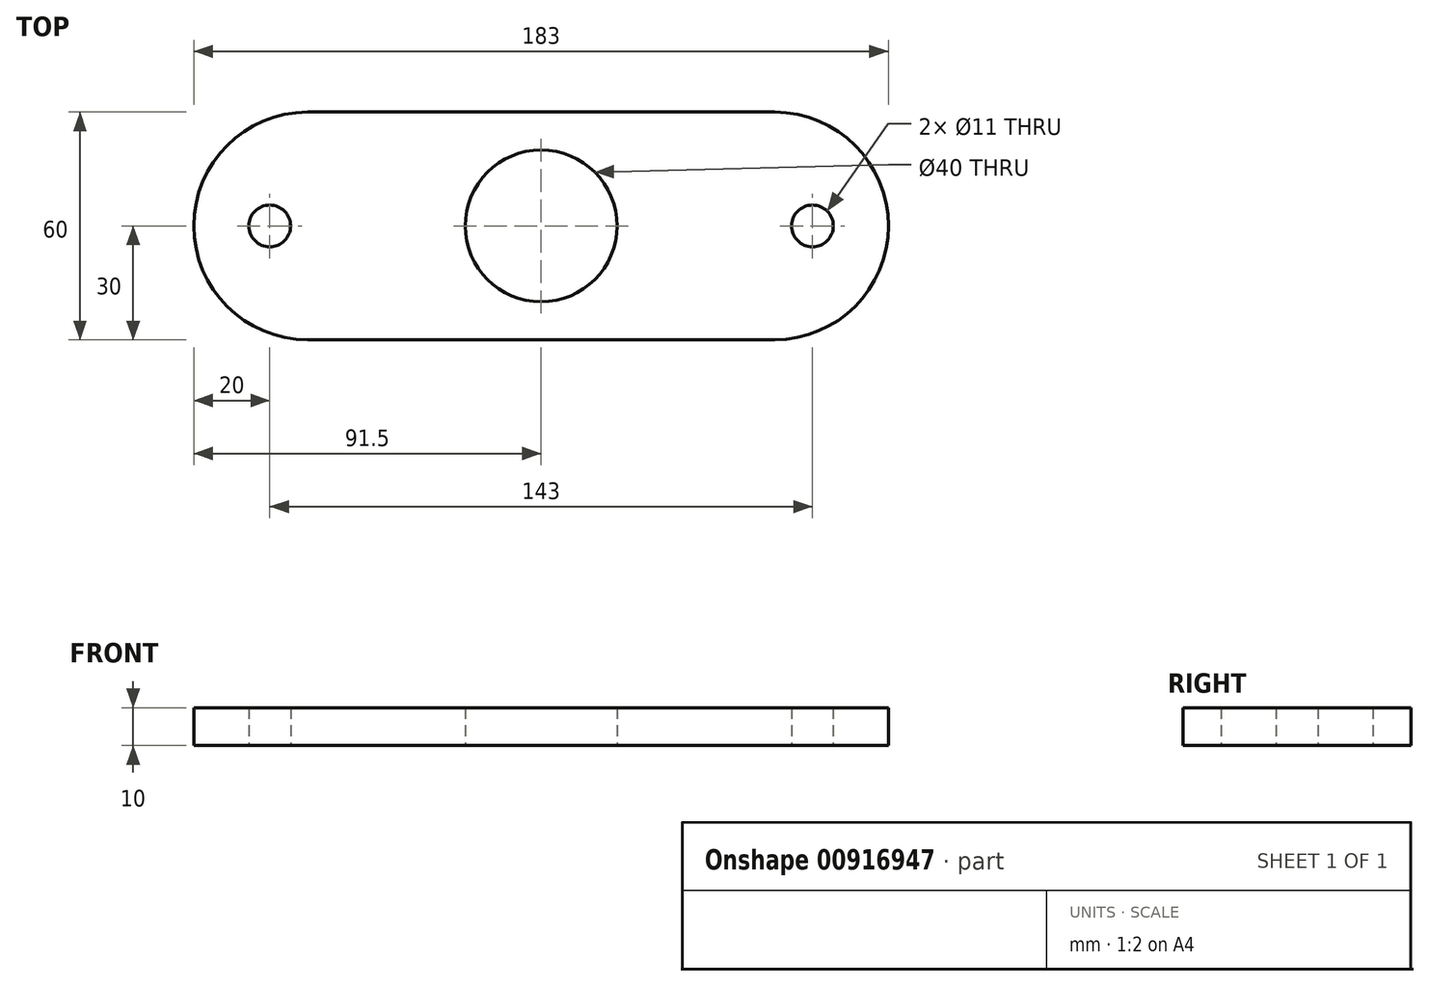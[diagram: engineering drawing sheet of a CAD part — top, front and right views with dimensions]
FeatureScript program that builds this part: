
annotation { "Feature Type Name" : "Feature", "Feature Type Description" : "" }
export const myFeature = defineFeature(function(context is Context, id is Id, definition is map)
    precondition{}
    {
        {
            var Q0;
            Q0=qCreatedBy(makeId("Top.planeOp"),FACE);
            var sketch = newSketch(context, id + "F0", { "sketchPlane" : qUnion([Q0])});
            skLineSegment(sketch, "E0.bottom", {"start": v(30, 0) * mm, "end": v(153, 0) * mm});
            skLineSegment(sketch, "E0.top", {"start": v(30, 60) * mm, "end": v(153, 60) * mm});
            skLineSegment(sketch, "E0.left", {"start": v(0, 30) * mm, "end": v(0, 30) * mm});
            skLineSegment(sketch, "E0.right", {"start": v(183, 30) * mm, "end": v(183, 30) * mm});
            skPoint(sketch, "E1.visualSharp", {"position": v(0, 60) * mm});
            skArc(sketch, "E1.filletArc", {"start": v(30, 60) * mm, "mid": v(8.79, 51.21) * mm, "end": v(0, 30) * mm});
            skPoint(sketch, "E2.visualSharp", {"position": v(0, 0) * mm});
            skArc(sketch, "E2.filletArc", {"start": v(0, 30) * mm, "mid": v(8.79, 8.79) * mm, "end": v(30, 0) * mm});
            skPoint(sketch, "E3.visualSharp", {"position": v(183, 60) * mm});
            skArc(sketch, "E3.filletArc", {"start": v(183, 30) * mm, "mid": v(174.21, 51.21) * mm, "end": v(153, 60) * mm});
            skPoint(sketch, "E4.visualSharp", {"position": v(183, 0) * mm});
            skArc(sketch, "E4.filletArc", {"start": v(153, 0) * mm, "mid": v(174.21, 8.79) * mm, "end": v(183, 30) * mm});
            skCircle(sketch, "E5", {"center": v(20, 30) * mm, "radius": 5.5 * mm});
            skCircle(sketch, "E6", {"center": v(163, 30) * mm, "radius": 5.5 * mm});
            skCircle(sketch, "E7", {"center": v(91.5, 30) * mm, "radius": 20 * mm});
            skPoint(sketch, "E7.centerSnap0", {"position": v(91.5, 60) * mm});
            skSolve(sketch);
        }
        {
            var Q0;
            Q0=makeQuery(id+"F0.imprint","IMPRINT",FACE,{"disambiguationData":[TD([[makeQuery(id+"F0.imprint","IMPRINT",EDGE,{"derivedFrom":sQuery(id+"F0.wireOp",EDGE,"E0.bottom")}),1.0]])]});
            extrude(context, id + "F1", {"entities" : qUnion([Q0]), "depth" : 10 * mm, "offsetDistance" : 25 * mm});
        }
    });
